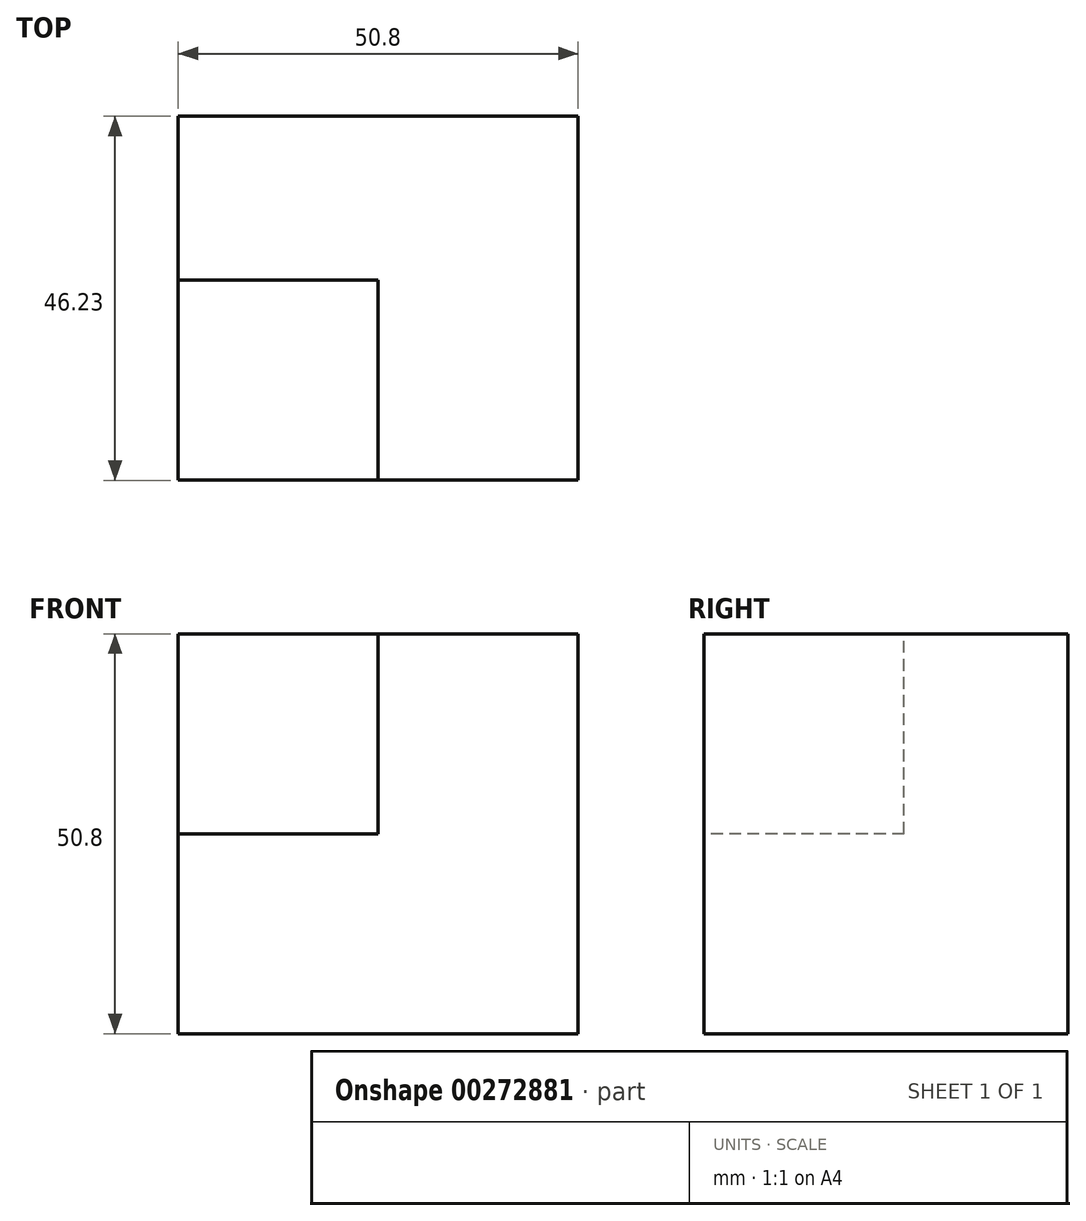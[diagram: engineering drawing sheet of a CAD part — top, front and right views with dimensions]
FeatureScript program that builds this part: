
annotation { "Feature Type Name" : "Feature", "Feature Type Description" : "" }
export const myFeature = defineFeature(function(context is Context, id is Id, definition is map)
    precondition{}
    {
        {
            var Q0;
            Q0=qCreatedBy(makeId("Front.planeOp"),FACE);
            var sketch = newSketch(context, id + "F0", { "sketchPlane" : qUnion([Q0])});
            skLineSegment(sketch, "E0", {"start": v(0, 0) * mm, "end": v(-50.8, 0) * mm});
            skLineSegment(sketch, "E1", {"start": v(-50.8, 0) * mm, "end": v(-50.8, 50.8) * mm});
            skLineSegment(sketch, "E2", {"start": v(-50.8, 50.8) * mm, "end": v(0, 50.8) * mm});
            skLineSegment(sketch, "E3", {"start": v(0, 50.8) * mm, "end": v(0, 0) * mm});
            skSolve(sketch);
        }
        {
            var Q0;
            Q0 = qSketchRegion(id + "F0", true);
            extrude(context, id + "F1", {"entities" : qUnion([Q0]), "depth" : 46.23 * mm});
        }
        {
            var Q0;
            Q0=makeQuery(id+"F1.opExtrude","CAP_FACE",FACE,{"disambiguationData":[OSD([sQuery(id+"F0.wireOp",EDGE,"E0"),sQuery(id+"F0.wireOp",EDGE,"E1"),sQuery(id+"F0.wireOp",EDGE,"E2"),sQuery(id+"F0.wireOp",EDGE,"E3")])],"isStart":false});
            var sketch = newSketch(context, id + "F2", { "sketchPlane" : qUnion([Q0])});
            skLineSegment(sketch, "E4.bottom", {"start": v(-50.8, 50.8) * mm, "end": v(-25.4, 50.8) * mm});
            skLineSegment(sketch, "E4.top", {"start": v(-50.8, 25.4) * mm, "end": v(-25.4, 25.4) * mm});
            skLineSegment(sketch, "E4.left", {"start": v(-50.8, 50.8) * mm, "end": v(-50.8, 25.4) * mm});
            skLineSegment(sketch, "E4.right", {"start": v(-25.4, 50.8) * mm, "end": v(-25.4, 25.4) * mm});
            skSolve(sketch);
        }
        {
            var Q0;
            Q0 = qSketchRegion(id + "F2", true);
            extrude(context, id + "F3", {"entities" : qUnion([Q0]), "operationType" : NewBodyOperationType.REMOVE, "oppositeDirection" : true, "depth" : 25.4 * mm});
        }
    });
